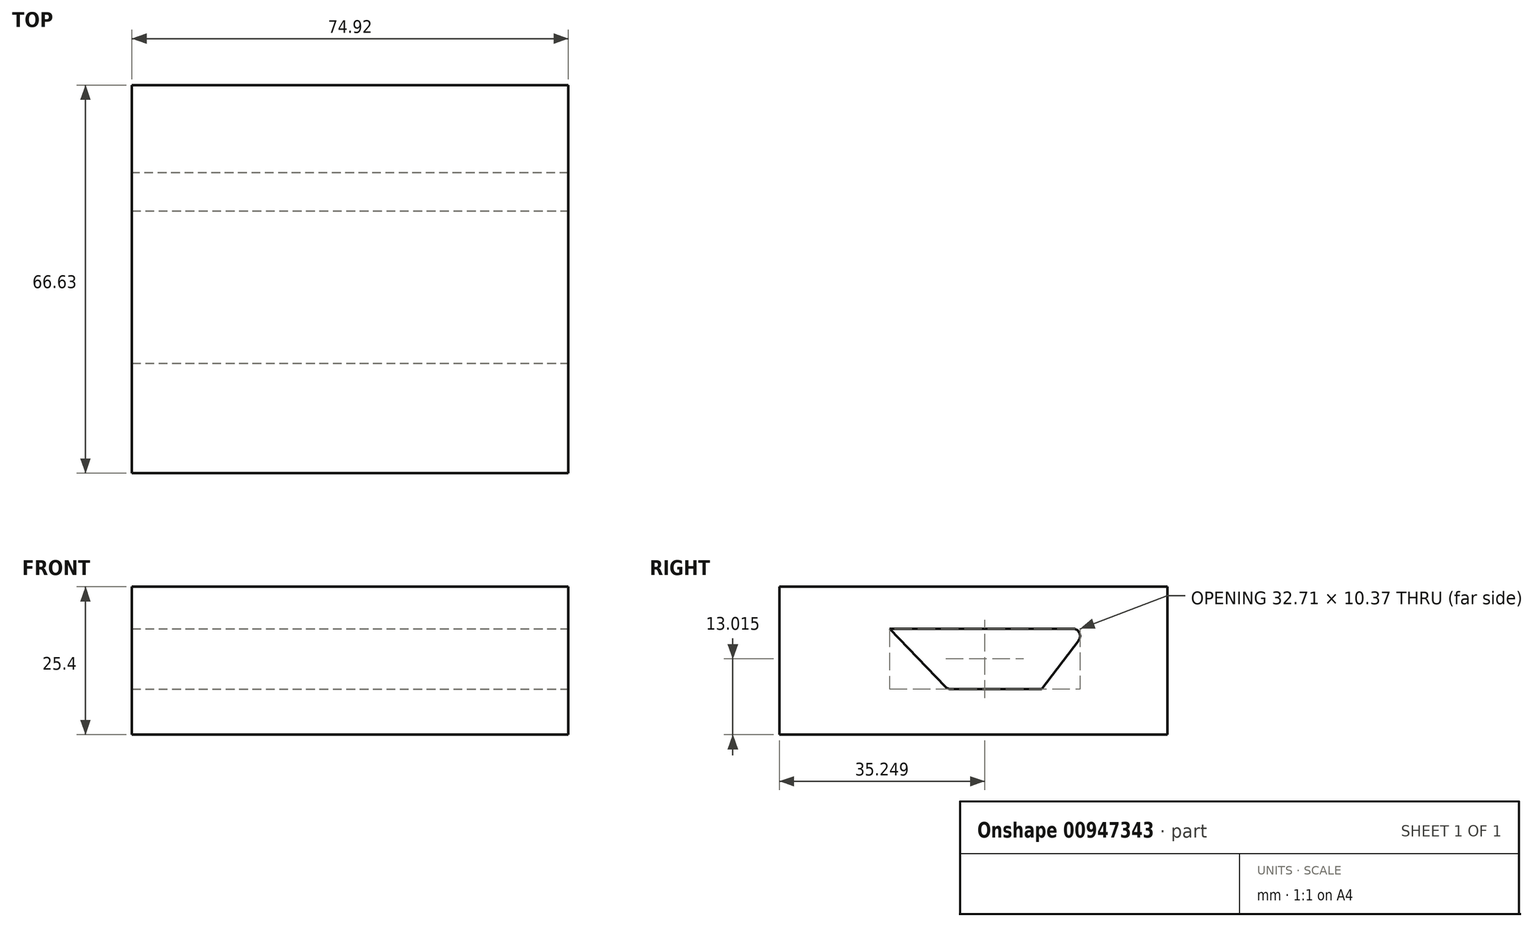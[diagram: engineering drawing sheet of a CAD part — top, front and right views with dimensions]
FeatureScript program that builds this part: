
annotation { "Feature Type Name" : "Feature", "Feature Type Description" : "" }
export const myFeature = defineFeature(function(context is Context, id is Id, definition is map)
    precondition{}
    {
        {
            var Q0;
            Q0=qCreatedBy(makeId("Top.planeOp"),FACE);
            var sketch = newSketch(context, id + "F0", { "sketchPlane" : qUnion([Q0])});
            skLineSegment(sketch, "E0.bottom", {"start": v(-42.22, -27.3) * mm, "end": v(32.7, -27.3) * mm});
            skLineSegment(sketch, "E0.top", {"start": v(-42.22, 39.33) * mm, "end": v(32.7, 39.33) * mm});
            skLineSegment(sketch, "E0.left", {"start": v(-42.22, -27.3) * mm, "end": v(-42.22, 39.33) * mm});
            skLineSegment(sketch, "E0.right", {"start": v(32.7, -27.3) * mm, "end": v(32.7, 39.33) * mm});
            skSolve(sketch);
        }
        {
            var Q0;
            Q0 = qSketchRegion(id + "F0", true);
            extrude(context, id + "F1", {"entities" : qUnion([Q0]), "depth" : 25.4 * mm, "offsetDistance" : 25.4 * mm});
        }
        {
            var Q0;
            Q0=makeQuery(id+"F1.opExtrude","SWEPT_FACE",FACE,{"disambiguationData":[OSD([sQuery(id+"F0.wireOp",EDGE,"E0.right")])]});
            var sketch = newSketch(context, id + "F2", { "sketchPlane" : qUnion([Q0])});
            skLineSegment(sketch, "E1", {"start": v(-8.4, 18.2) * mm, "end": v(25.6, 18.2) * mm});
            skLineSegment(sketch, "E2", {"start": v(25.6, 18.2) * mm, "end": v(17.72, 7.83) * mm});
            skLineSegment(sketch, "E3", {"start": v(17.72, 7.83) * mm, "end": v(1.58, 7.83) * mm});
            skLineSegment(sketch, "E4", {"start": v(1.58, 7.83) * mm, "end": v(-8.4, 18.2) * mm});
            skSolve(sketch);
        }
        {
            var Q0;
            Q0 = qSketchRegion(id + "F2", true);
            extrude(context, id + "F3", {"entities" : qUnion([Q0]), "operationType" : NewBodyOperationType.REMOVE, "oppositeDirection" : true, "depth" : 84.07 * mm, "offsetDistance" : 25.4 * mm});
        }
        {
            var Q0;
            Q0=makeQuery(id+"F3.boolean.opBoolean","COPY",EDGE,{"derivedFrom":makeQuery(id+"F3.opExtrude","SWEPT_EDGE",EDGE,{"disambiguationData":[OSD([sQuery(id+"F2.wireOp",EDGE,"E3"),sQuery(id+"F2.wireOp",EDGE,"E4")])]})});
            var Q1;
            Q1=makeQuery(id+"F3.boolean.opBoolean","COPY",EDGE,{"derivedFrom":makeQuery(id+"F3.opExtrude","SWEPT_EDGE",EDGE,{"disambiguationData":[OSD([sQuery(id+"F2.wireOp",EDGE,"E1"),sQuery(id+"F2.wireOp",EDGE,"E2")])]})});
            fillet(context, id + "F4", {"entities" : qUnion([Q0, Q1]), "radius" : 1.27 * mm, "tangentPropagation" : true, "allowEdgeOverflow" : false});
        }
    });
